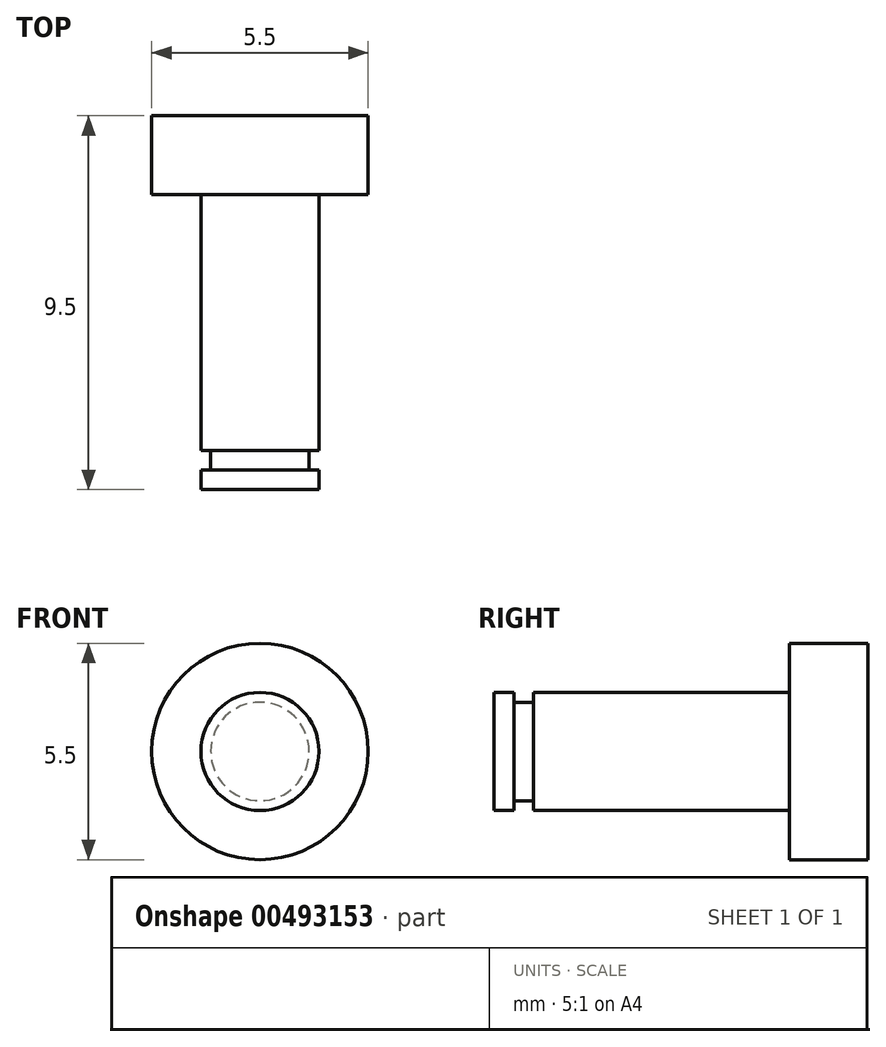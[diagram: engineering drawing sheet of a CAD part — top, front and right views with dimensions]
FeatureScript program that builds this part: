
annotation { "Feature Type Name" : "Feature", "Feature Type Description" : "" }
export const myFeature = defineFeature(function(context is Context, id is Id, definition is map)
    precondition{}
    {
        {
            var Q0;
            Q0=qCreatedBy(makeId("Front.planeOp"),FACE);
            var sketch = newSketch(context, id + "F0", { "sketchPlane" : qUnion([Q0])});
            skCircle(sketch, "E0", {"center": v(0, 0) * mm, "radius": 2.75 * mm});
            skSolve(sketch);
        }
        {
            var Q0;
            Q0=qSketchRegion(id+"F0",true);
            extrude(context, id + "F1", {"entities" : qUnion([Q0]), "depth" : 2 * mm});
        }
        {
            var Q0;
            Q0=makeQuery(id+"F1.opExtrude","CAP_FACE",FACE,{"disambiguationData":[OSD([sQuery(id+"F0.wireOp",EDGE,"E0")])],"isStart":false});
            var sketch = newSketch(context, id + "F2", { "sketchPlane" : qUnion([Q0])});
            skCircle(sketch, "E1", {"center": v(0, 0) * mm, "radius": 1.5 * mm});
            skSolve(sketch);
        }
        {
            var Q0;
            Q0=qSketchRegion(id+"F2",true);
            extrude(context, id + "F3", {"entities" : qUnion([Q0]), "operationType" : NewBodyOperationType.ADD, "depth" : 6.5 * mm});
        }
        {
            var Q0;
            Q0=makeQuery(id+"F3.opExtrude","CAP_FACE",FACE,{"disambiguationData":[OSD([sQuery(id+"F2.wireOp",EDGE,"E1")])],"isStart":false});
            var sketch = newSketch(context, id + "F4", { "sketchPlane" : qUnion([Q0])});
            skCircle(sketch, "E2", {"center": v(0, 0) * mm, "radius": 1.25 * mm});
            skSolve(sketch);
        }
        {
            var Q0;
            Q0=qSketchRegion(id+"F4",true);
            extrude(context, id + "F5", {"entities" : qUnion([Q0]), "operationType" : NewBodyOperationType.ADD, "depth" : .5 * mm});
        }
        {
            var Q0;
            Q0=makeQuery(id+"F5.opExtrude","CAP_FACE",FACE,{"disambiguationData":[OSD([sQuery(id+"F4.wireOp",EDGE,"E2")])],"isStart":false});
            var sketch = newSketch(context, id + "F6", { "sketchPlane" : qUnion([Q0])});
            skCircle(sketch, "E3", {"center": v(0, 0) * mm, "radius": 1.5 * mm});
            skSolve(sketch);
        }
        {
            var Q0;
            Q0=qSketchRegion(id+"F6",true);
            extrude(context, id + "F7", {"entities" : qUnion([Q0]), "operationType" : NewBodyOperationType.ADD, "depth" : .5 * mm});
        }
    });
